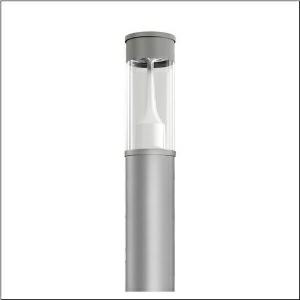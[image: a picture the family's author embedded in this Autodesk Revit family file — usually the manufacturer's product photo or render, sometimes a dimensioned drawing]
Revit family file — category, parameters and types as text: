
# Revit family: city-light_400_iq___st1_2a_5xa5305kf14hp_bbb3
name_source: partatom
category: Lighting Fixtures
units: mm (PartAtom-declared; Revit-internal decimal feet)

## family parameters
Cut with Voids When Loaded = No
Host = Face
Light Source = No
Part Type = Normal
Room Calculation Point = No
Round Connector Dimension = Use Diameter
Shared = No

## types (1)
- --- (1 x LED, 4940 lm, 33.6 W, 4000K)
    Apparent Load = 34 VA
    CIE Flux Codes = 22 61 94 96 100
    Color Rendering = 70
    Color Temperature = 4000K
    Default Elevation = 1800 mm
    Description = City-Light 400 iQ, light pillar, Module 540 iQ-SR, primary light control with 3 zone facetted reflector, of plastic, silver coated, highly specular, structured, primary optical cover: cover, of PMMA, transparent, partly coated, light distribution: ST1.2a, primary light characteristic: asymmetric, LED, High Power LED, rated luminous flux: 4.940lm, luminous efficacy: 147lm/W, light colour: 740, colour temperature: 4000K, control gear: iQ Street-Remote, control: pre-setting: logarithmic dimming characteristic, Street-Remote, Auto-Match, Temp-Guard, Lumen-Switch, Night-Set, Smart-Wire, Light-Fading, Desk-Remote (wireless, voltage-free reading and setting of iQ features in the workshop via application-optimized NFC function/RFID function), optimised constant luminous flux control (CLO 2.0), with terminal, 6-pole, max. 2.5mm², mains connection: 230..240V, AC, 50/60Hz, start of lifetime: 34W, end of service life: 36W, reduction: 15W, luminaire housing, cylindrical, of extruded aluminium section, coated, Siteco® metallic grey (DB 702S), length: 4.694mm, diameter: 200mm, Module 540 iQ-SR, traffic white (RAL 9016), equipment: Power, protection rating (complete): IP65, insulation class (complete): insulation class II (safety insulation), certification: CE, ENEC, VDE, packaging unit: 1 piece

Light Distribution: ST1.2a
    Height = 500 mm
    Lamp = 1 x LED
    Lamp Light Flux = 4940 lm
    Lamp Power = 33.6 W
    Lamp count = 1
    Length = 200 mm  [stored 0.656168 ft]
    Luminous efficacy = 147 lm/W
    Manufacturer = Siteco
    ModVariant = No
    Model = 5XA5305KF14HP
    Mounting Place = Floor
    Mounting Type = Freestanding
    Number of Poles = 1
    OnlyDefault = Yes
    Power Factor = 1
    Product Name = City-Light 400 iQ | ST1.2a
    Product group = light pillar
    ProductGroupID = 1301
    Protection Class = Protection class II
    Protection Degree = IP 65
    RLX_Detail_Level = 1
    RLX_Emergency_Light_Flux = 0 lm
    RLX_Emergency_Type = 0
    RLX_Emergency_Type_DB = No
    RlxData = <blob elided: 53493 chars, md5=0fb753ad>
    Socket = socket
    Standby Power = 0 W
    System Light Flux = 4940 lm
    System Power = 34 W
    Type Comments = factory setting: luminous flux: 100 % | dim-lin: 254 | 695 mA
    Type Image = l_1006916.jpg
    URL = http://relux.com
    VarID = @adj_190287
    Voltage = 0 V
    Weight = 0.00 kg
    Width = 0 mm  [stored 0 ft]

note: [stored X ft] marks values corroborated as IEEE doubles in the binary element streams (Revit-internal decimal feet)

## geometry (parser evidence)
native form markers: Blend x4, Sweep x12
no freeform markers — native parametric forms only
